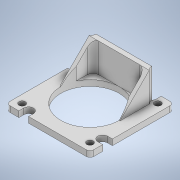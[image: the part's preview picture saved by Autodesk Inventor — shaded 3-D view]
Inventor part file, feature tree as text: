
AUTODESK INVENTOR PART (.ipt)
format: ipt  version: 2020.1 (Build 241239000, 239)  size: 200,192 bytes
history: native  units: mm
features: extrude x2, sketch x2, other x1, chamfer x1, fillet x1
ambient origin geometry x8: Origin, YZ Plane, XZ Plane, XY Plane, X Axis, Y Axis, Z Axis, Center Point
bodies: Body1 (feature_tree)
feature tree (7):
  other  "Твердое тело1"
  extrude  "Выдавливание1"  Depth=6.0mm TaperAngle=0.0deg
  extrude  "Выдавливание3"  Depth=4.8mm
  chamfer  "Фаска1"  Distance=8.0mm
  fillet  "Сопряжение1"  Radius=30.0mm
  sketch  "Эскиз1"
  sketch  "Эскиз2"
